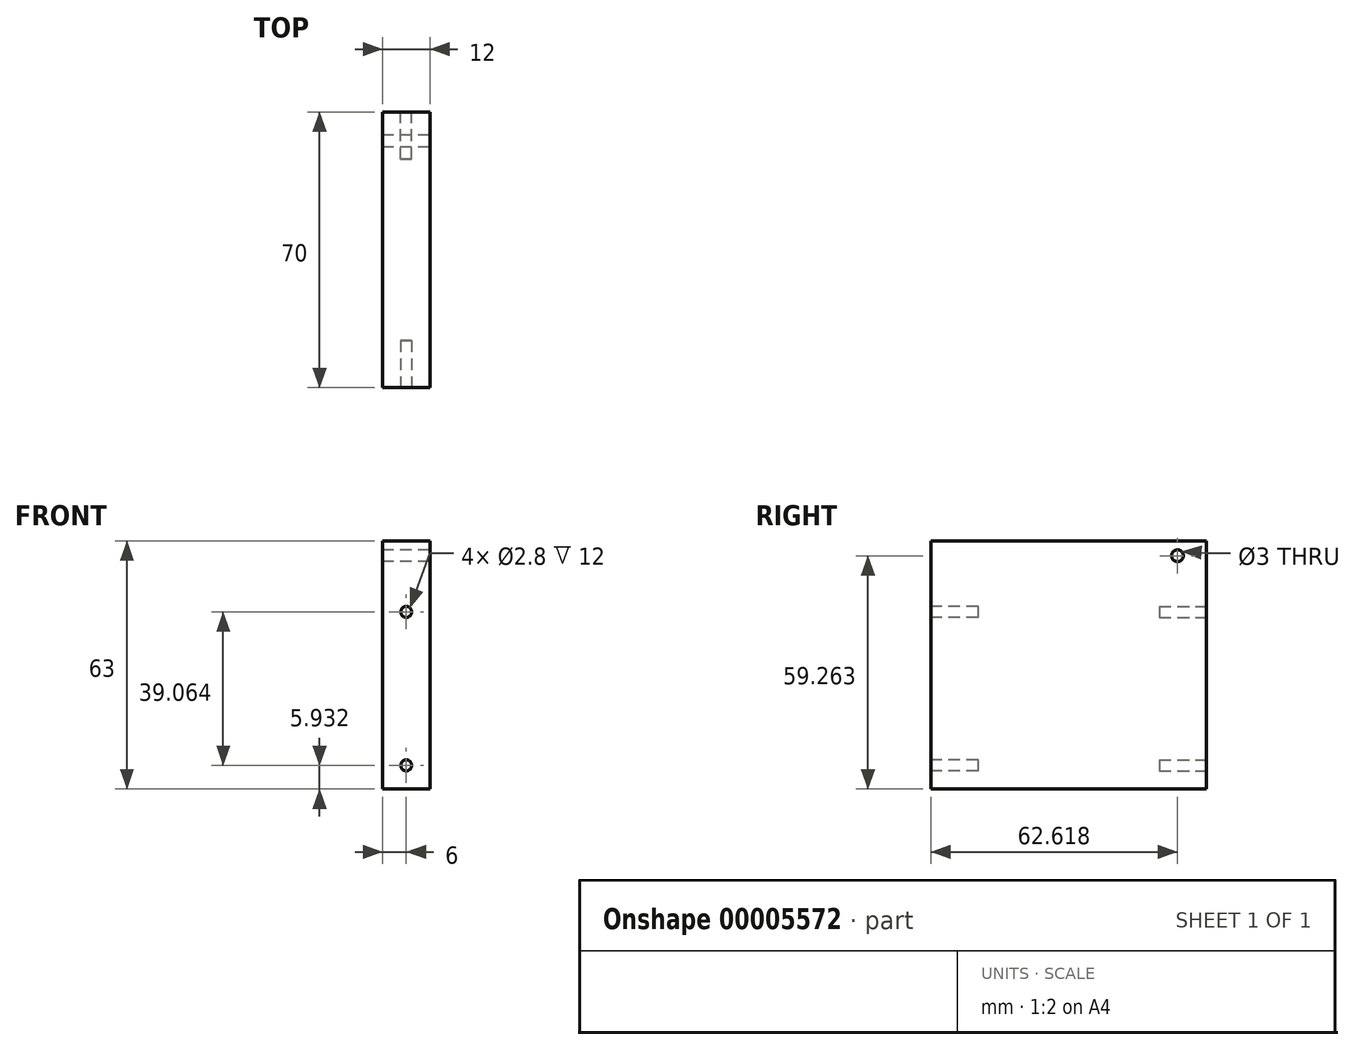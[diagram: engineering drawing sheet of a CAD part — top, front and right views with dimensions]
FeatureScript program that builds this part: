
annotation { "Feature Type Name" : "Feature", "Feature Type Description" : "" }
export const myFeature = defineFeature(function(context is Context, id is Id, definition is map)
    precondition{}
    {
        {
            var Q0;
            Q0=qCreatedBy(makeId("Right.planeOp"),FACE);
            var sketch = newSketch(context, id + "F0", { "sketchPlane" : qUnion([Q0])});
            skLineSegment(sketch, "E0.bottom", {"start": v(-34.17, 35.3) * mm, "end": v(35.83, 35.3) * mm});
            skLineSegment(sketch, "E0.top", {"start": v(-34.17, -30.7) * mm, "end": v(35.83, -30.7) * mm});
            skLineSegment(sketch, "E0.left", {"start": v(-34.17, 35.3) * mm, "end": v(-34.17, -30.7) * mm});
            skLineSegment(sketch, "E0.right", {"start": v(35.83, 35.3) * mm, "end": v(35.83, -30.7) * mm});
            skCircle(sketch, "E1", {"center": v(28.45, 28.56) * mm, "radius": 1.5 * mm});
            skSolve(sketch);
        }
        {
            var Q0;
            Q0=makeQuery(id+"F0.imprint","IMPRINT",FACE,{"disambiguationData":[TD([[makeQuery(id+"F0.imprint","IMPRINT",EDGE,{"derivedFrom":sQuery(id+"F0.wireOp",EDGE,"E0.bottom")}),-1.0]])]});
            extrude(context, id + "F1", {"entities" : qUnion([Q0]), "depth" : 12 * mm});
        }
        {
            var Q0;
            Q0=makeQuery(id+"F1.opExtrude","SWEPT_FACE",FACE,{"disambiguationData":[OSD([sQuery(id+"F0.wireOp",EDGE,"E0.left")])]});
            var sketch = newSketch(context, id + "F2", { "sketchPlane" : qUnion([Q0])});
            skCircle(sketch, "E2", {"center": v(6, -24.7) * mm, "radius": 1.4 * mm});
            skCircle(sketch, "E3", {"center": v(6, 14.3) * mm, "radius": 1.4 * mm});
            skLineSegment(sketch, "E4", {"start": v(6, -24.7) * mm, "end": v(6, 14.3) * mm, "construction": true});
            skSolve(sketch);
        }
        {
            var Q0;
            {Q0=qUnion([makeQuery(id+"F2.imprint","IMPRINT",FACE,{"disambiguationData":[TD([[makeQuery(id+"F2.imprint","IMPRINT",EDGE,{"derivedFrom":sQuery(id+"F2.wireOp",EDGE,"E2")}),1.0]])]}),makeQuery(id+"F2.imprint","IMPRINT",FACE,{"disambiguationData":[TD([[makeQuery(id+"F2.imprint","IMPRINT",EDGE,{"derivedFrom":sQuery(id+"F2.wireOp",EDGE,"E3")}),1.0]])]})]);}
            extrude(context, id + "F3", {"entities" : qUnion([Q0]), "operationType" : NewBodyOperationType.REMOVE, "oppositeDirection" : true, "depth" : 12 * mm});
        }
        {
            var Q0;
            Q0=makeQuery(id+"F1.opExtrude","SWEPT_FACE",FACE,{"disambiguationData":[OSD([sQuery(id+"F0.wireOp",EDGE,"E0.right")])]});
            var sketch = newSketch(context, id + "F4", { "sketchPlane" : qUnion([Q0])});
            skCircle(sketch, "E5", {"center": v(-6, -24.77) * mm, "radius": 1.4 * mm});
            skCircle(sketch, "E6", {"center": v(-6, 14.3) * mm, "radius": 1.4 * mm});
            skSolve(sketch);
        }
        {
            var Q0;
            {Q0=qUnion([makeQuery(id+"F4.imprint","IMPRINT",FACE,{"disambiguationData":[TD([[makeQuery(id+"F4.imprint","IMPRINT",EDGE,{"derivedFrom":sQuery(id+"F4.wireOp",EDGE,"E5")}),1.0]])]}),makeQuery(id+"F4.imprint","IMPRINT",FACE,{"disambiguationData":[TD([[makeQuery(id+"F4.imprint","IMPRINT",EDGE,{"derivedFrom":sQuery(id+"F4.wireOp",EDGE,"E6")}),1.0]])]})]);}
            extrude(context, id + "F5", {"entities" : qUnion([Q0]), "operationType" : NewBodyOperationType.REMOVE, "oppositeDirection" : true, "depth" : 12 * mm});
        }
        {
            var Q0;
            Q0=makeQuery(id+"F1.opExtrude","CAP_FACE",FACE,{"disambiguationData":[OSD([sQuery(id+"F0.wireOp",EDGE,"E0.bottom"),sQuery(id+"F0.wireOp",EDGE,"E0.top"),sQuery(id+"F0.wireOp",EDGE,"E0.left"),sQuery(id+"F0.wireOp",EDGE,"E0.right"),sQuery(id+"F0.wireOp",EDGE,"E1")])],"isStart":false});
            var sketch = newSketch(context, id + "F6", { "sketchPlane" : qUnion([Q0])});
            skLineSegment(sketch, "E7.bottom", {"start": v(-34.17, 35.3) * mm, "end": v(35.83, 35.3) * mm});
            skLineSegment(sketch, "E7.top", {"start": v(-34.17, 32.3) * mm, "end": v(35.83, 32.3) * mm});
            skLineSegment(sketch, "E7.left", {"start": v(-34.17, 35.3) * mm, "end": v(-34.17, 32.3) * mm});
            skLineSegment(sketch, "E7.right", {"start": v(35.83, 35.3) * mm, "end": v(35.83, 32.3) * mm});
            skSolve(sketch);
        }
        {
            var Q0;
            Q0=makeQuery(id+"F6.imprint","IMPRINT",FACE,{"disambiguationData":[TD([[makeQuery(id+"F6.imprint","IMPRINT",EDGE,{"derivedFrom":sQuery(id+"F6.wireOp",EDGE,"E7.bottom")}),-1.0]])]});
            var Q1;
            Q1=makeQuery(id+"F1.opExtrude","CAP_FACE",FACE,{"disambiguationData":[OSD([sQuery(id+"F0.wireOp",EDGE,"E0.bottom"),sQuery(id+"F0.wireOp",EDGE,"E0.top"),sQuery(id+"F0.wireOp",EDGE,"E0.left"),sQuery(id+"F0.wireOp",EDGE,"E0.right"),sQuery(id+"F0.wireOp",EDGE,"E1")])],"isStart":true});
            extrude(context, id + "F7", {"entities" : qUnion([Q0]), "operationType" : NewBodyOperationType.REMOVE, "endBound" : BoundingType.UP_TO_SURFACE, "oppositeDirection" : true, "endBoundEntityFace" : qUnion([Q1]), "depth" : 25 * mm});
        }
    });
